# Revit family: BE_84766_de_DE
name_source: partatom
category: Leuchten
units: mm (PartAtom-declared; Revit-internal decimal feet)

## family parameters
Basisbauteil = Fläche
Beim Laden mit Abzugskörper schneiden = Ja
Bemaßung runder Anschluss = Durchmesser verwenden
Gemeinsam genutzt = Nein
Lichtquelle = Ja
Raumberechnungspunkt = Ja
Teiletyp = Normal

## types (6) — shared parameters
AC/DC = AC/DC
Aktualisierung = 2022-05-19T04:00:07
Anschlussleitung = 1.8 m 07RN8-F 3 G 1²
BEGA_Dummy = Nein
BEGA_IES = Ja
BEGA_Intern = Ja
BEGA_Intern_Konstruktion = Ja
BEGA_Intern_an = Ja
BEGA_Intern_aus = Ja
Beschreibung = Bodeneinbauleuchte
Beschreibung_Sonderanfertigung = Hier können Sie Informationen zur Sonderanfertigung eintragen.
CE_Konformität = ja
ENEC = ja
Einbaugehäuse = Nein
Einbautiefe = 160 mm
Energieeffizienzklasse = LED A++ - A
Farbfilter = 16777215
Farbtemperaturverschiebung bei Dämpfen der Lampe = <Keine Auswahl>
Farbwiedergabeindex = CRI > 80
Frequenz = 0/50-60 Hz
Gewicht = 1.9 kg
Hersteller = BEGA
Lampe = LED 4 W
Lastklassifizierung = Beleuchtung
Lebensdauerkriterien = L70B50 @ 25 °C = 145000 h
Logo = BEGA_Logo.png
M_A = Nein
M_G = Nein
M_W = Nein
Material_03 = BEGA_Oberfläche_Weiss_matt
Material_05 = BEGA_Oberfläche_Aluminium Guss
Material_06 = BEGA_Oberfläche_Edelstahl_gebürstet
Material_09 = BEGA_Glas_klar
Material_13 = BEGA_Kunststoff_matt
Material_15 = BEGA_Leuchtmedium_matt
Material_17 = BEGA_Reflektor
Material_18 = BEGA_Gummi_schwarz
Neigungswinkel = 0.00°
Oberflächentemperatur = 25 °C
Produktdatenblatt = https://cdn.bega.com
Scheinlast = 0 VA
Schutzart = IP 68...10m
Schutzklasse = I
Sonderanfertigung = Nein
Spannung = 240 V
URL = https://www.bega.com
Umgebungstemperatur = 25 °C
zero-valued in all types: Vorgabe-Ansicht

## per-type parameters (varying)
| type | Bestellnummer | Datei für fotometrisches Netz | Farbtemperatur | LED_Modulbezeichnung | Lampenlichtstrom | Leuchtenlichtstrom | Modell | Rutschhemmendes_Glas |
| BEGA_84766_R_K4 | 84766RK4 | BE_84766RK4.IES | 4000 K | LED-1120/840 | 705 lm | 432 lm | 84766RK4 | ja |
| BEGA_84766_R_K3 | 84766RK3 | BE_84766RK3.IES | 3000 K | LED-1120/830 | 675 lm | 414 lm | 84766RK3 | ja |
| BEGA_84766_K4 | 84766K4 | BE_84766K4.IES | 4000 K | LED-1120/840 | 705 lm | 432 lm | 84766K4 |  |
| BEGA_84766_K3 | 84766K3 | BE_84766K3.IES | 3000 K | LED-1120/830 | 675 lm | 414 lm | 84766K3 |  |
| BEGA_84766_R_K27 | 84766RK27 | BE_84766RK27.IES | 2700 K | LED-1120/827 | 655 lm | 402 lm | 84766RK27 | ja |
| BEGA_84766_K27 | 84766K27 | BE_84766K27.IES | 2700 K | LED-1120/827 | 655 lm | 402 lm | 84766K27 | ja |
